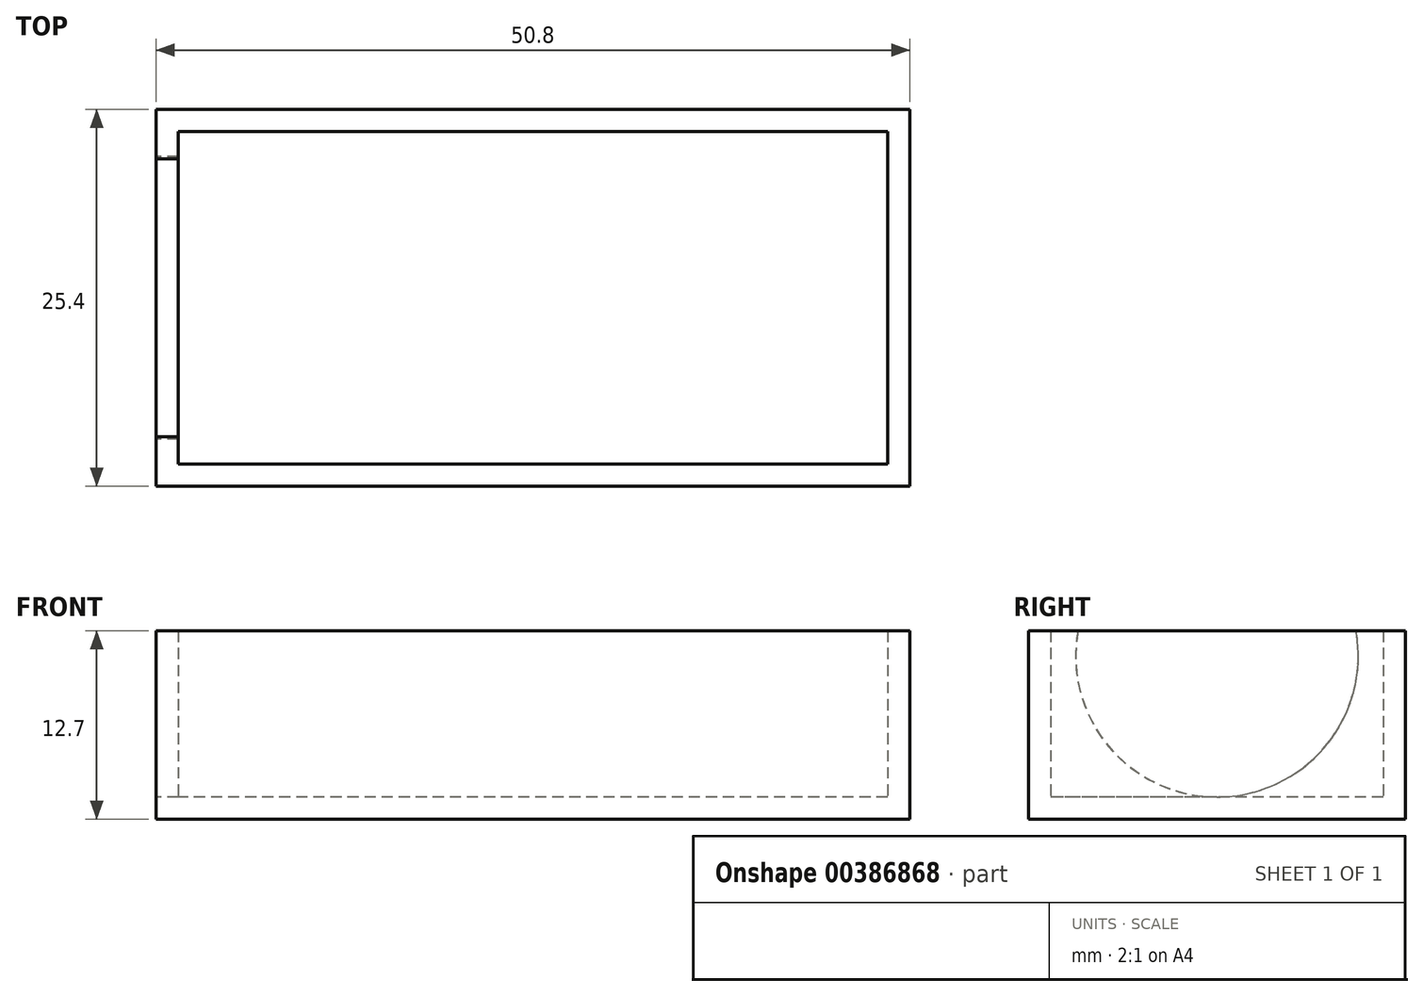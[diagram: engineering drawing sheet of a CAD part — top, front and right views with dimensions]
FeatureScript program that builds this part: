
annotation { "Feature Type Name" : "Feature", "Feature Type Description" : "" }
export const myFeature = defineFeature(function(context is Context, id is Id, definition is map)
    precondition{}
    {
        {
            var Q0;
            Q0=qCreatedBy(makeId("Top.planeOp"),FACE);
            var sketch = newSketch(context, id + "F0", { "sketchPlane" : qUnion([Q0])});
            skLineSegment(sketch, "E0.bottom", {"start": v(25.4, 12.7) * mm, "end": v(-25.4, 12.7) * mm});
            skLineSegment(sketch, "E0.top", {"start": v(25.4, -12.7) * mm, "end": v(-25.4, -12.7) * mm});
            skLineSegment(sketch, "E0.left", {"start": v(25.4, 12.7) * mm, "end": v(25.4, -12.7) * mm});
            skLineSegment(sketch, "E0.right", {"start": v(-25.4, 12.7) * mm, "end": v(-25.4, -12.7) * mm});
            skPoint(sketch, "E0.middle", {"position": v(0, 0) * mm});
            skSolve(sketch);
        }
        {
            var Q0;
            Q0=makeQuery(id+"F0.imprint","IMPRINT",FACE,{"disambiguationData":[TD([[makeQuery(id+"F0.imprint","IMPRINT",EDGE,{"derivedFrom":sQuery(id+"F0.wireOp",EDGE,"E0.bottom")}),1.0]])]});
            extrude(context, id + "F1", {"entities" : qUnion([Q0]), "depth" : 12.7 * mm});
        }
        {
            var Q0;
            Q0=makeQuery(id+"F1.opExtrude","CAP_FACE",FACE,{"disambiguationData":[OSD([sQuery(id+"F0.wireOp",EDGE,"E0.bottom"),sQuery(id+"F0.wireOp",EDGE,"E0.top"),sQuery(id+"F0.wireOp",EDGE,"E0.left"),sQuery(id+"F0.wireOp",EDGE,"E0.right")])],"isStart":false});
            shell(context, id + "F2", {"entities" : qUnion([Q0]), "thickness" : 1.5 * mm});
        }
        {
            var Q0;
            Q0=makeQuery(id+"F1.opExtrude","SWEPT_FACE",FACE,{"disambiguationData":[OSD([sQuery(id+"F0.wireOp",EDGE,"E0.right")])]});
            var sketch = newSketch(context, id + "F3", { "sketchPlane" : qUnion([Q0])});
            skCircle(sketch, "E1", {"center": v(0, 11.03) * mm, "radius": 9.53 * mm});
            skSolve(sketch);
        }
        {
            var Q0;
            {var subQ0=sQuery(id+"F3.wireOp",EDGE,"E1");var subQ1=makeQuery(id+"F1.opExtrude","CAP_EDGE",EDGE,{"disambiguationData":[OSD([sQuery(id+"F0.wireOp",EDGE,"E0.right")])],"isStart":false});var subQ2=makeQuery(id+"F3.imprint","INTERSECT",VERTEX,{"disambiguationData":[OD(0.0)],"derivedFrom":[subQ1,subQ0]});Q0=makeQuery(id+"F3.imprint","IMPRINT",FACE,{"disambiguationData":[TD([[makeQuery(id+"F3.imprint","IMPRINT",EDGE,{"disambiguationData":[TD([[subQ2,-1.0]])],"derivedFrom":subQ0}),1.0]])]});}
            extrude(context, id + "F4", {"entities" : qUnion([Q0]), "operationType" : NewBodyOperationType.REMOVE, "oppositeDirection" : true, "depth" : 1.5 * mm});
        }
    });
